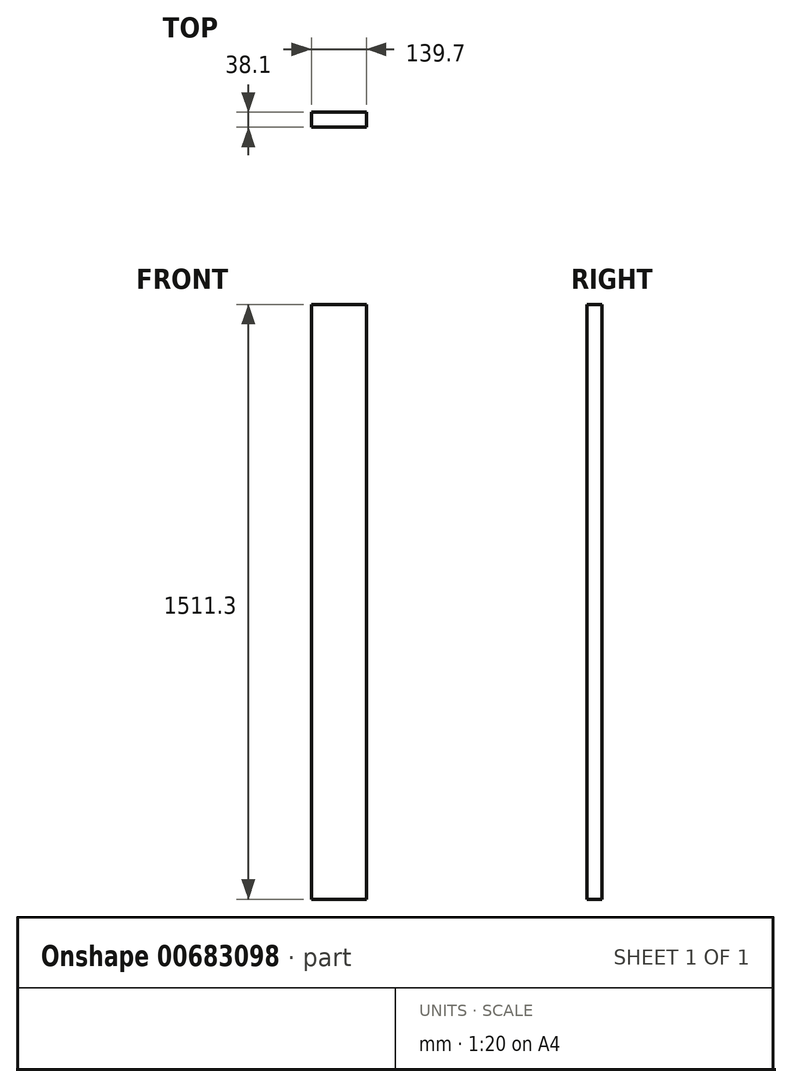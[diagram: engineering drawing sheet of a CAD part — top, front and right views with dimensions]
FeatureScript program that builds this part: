
annotation { "Feature Type Name" : "Feature", "Feature Type Description" : "" }
export const myFeature = defineFeature(function(context is Context, id is Id, definition is map)
    precondition{}
    {
        {
            var Q0;
            Q0=qCreatedBy(makeId("Top.planeOp"),FACE);
            var sketch = newSketch(context, id + "F0", { "sketchPlane" : qUnion([Q0])});
            skLineSegment(sketch, "E0.bottom", {"start": v(69.85, 19.05) * mm, "end": v(-69.85, 19.05) * mm});
            skLineSegment(sketch, "E0.top", {"start": v(69.85, -19.05) * mm, "end": v(-69.85, -19.05) * mm});
            skLineSegment(sketch, "E0.left", {"start": v(69.85, 19.05) * mm, "end": v(69.85, -19.05) * mm});
            skLineSegment(sketch, "E0.right", {"start": v(-69.85, 19.05) * mm, "end": v(-69.85, -19.05) * mm});
            skPoint(sketch, "E0.middle", {"position": v(0, 0) * mm});
            skSolve(sketch);
        }
        {
            var Q0;
            Q0=makeQuery(id+"F0.imprint","IMPRINT",FACE,{"disambiguationData":[TD([[makeQuery(id+"F0.imprint","IMPRINT",EDGE,{"derivedFrom":sQuery(id+"F0.wireOp",EDGE,"E0.bottom")}),1.0]])]});
            extrude(context, id + "F1", {"entities" : qUnion([Q0]), "depth" : 1511.3 * mm, "offsetDistance" : 25.4 * mm});
        }
    });
